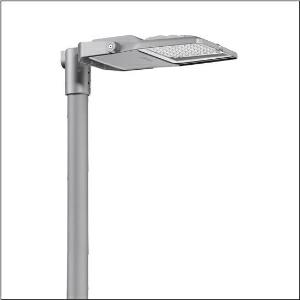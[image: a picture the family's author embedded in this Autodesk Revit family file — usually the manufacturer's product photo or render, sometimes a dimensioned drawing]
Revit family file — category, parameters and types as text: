
# Revit family: floodlight_fl_21_iq_mini___pl43_5xa7772b4a3a_1e53
name_source: partatom
category: Lighting Fixtures
units: mm (PartAtom-declared; Revit-internal decimal feet)

## family parameters
Cut with Voids When Loaded = No
Host = Face
Light Source = No
Part Type = Normal
Room Calculation Point = No
Round Connector Dimension = Use Diameter
Shared = No

## types (1)
- --- (1 x LED, 6660 lm, 45.5 W, 4000K)
    Apparent Load = 46 VA
    CIE Flux Codes = 27 78 99 100 100
    Color Rendering = 70
    Color Temperature = 4000K
    Default Elevation = 1800 mm
    Description = Floodlight FL 21 iQ mini, floodlight, primary light control with lens, of PMMA, primary optical cover: protective disc, of toughened safety glass, transparent, light distribution: PL43, light emission: direct distribution, installation type: surface-mounted, LED, High Power LED, rated luminous flux: 6.660lm, luminous efficacy: 146lm/W, light colour: 740, colour temperature: 4000K, control: Auto-Match, Temp-Guard, Night-Set, Smart-Wire, Desk-Remote (wireless, voltage-free reading and setting of iQ features in the workshop via application-optimized NFC function/RFID function), optimised constant luminous flux control (CLO 2.0), Light-Fading, Lumen-Switch, with terminal, 6-pole, mains connection: 220..240V, AC, 50/60Hz, start of lifetime: 46W, end of service life: 48W, reduction: 22W, luminaire housing, of diecast aluminium, powder-coated, Siteco® metallic grey (DB 702S), corrosivity category C5 mid according to DIN EN ISO 12944, sealing non-destructively replaceable, please order mast flange separately, mast bracket, of steel, galvanised, powder-coated, protection rating (complete): IP66, insulation class (complete): insulation class II (safety insulation), certification: CE, ENEC, VDE, protection symbol: D, impact resistance: IK08, permissible operating ambient temperature: -40..+40°C, permissible operating ambient temperature for outdoor applications: -40..+50°C, standard: DIN EN 12944, LABS conformity tested according to VDMA 24364:2018-05, packaging unit: 1 piece

Light Distribution: PL43
    Height = 70 mm
    Lamp = 1 x LED
    Lamp Light Flux = 6660 lm
    Lamp Power = 45.5 W
    Lamp count = 1
    Length = 485 mm
    Luminous efficacy = 146 lm/W
    Manufacturer = Siteco
    ModVariant = No
    Model = 5XA7772B4A3A
    Number of Poles = 1
    OnlyDefault = Yes
    Power Factor = 1
    Product Name = Floodlight FL 21 iQ mini | PL43
    Product group = floodlight | pylon annexe
    ProductGroupID = 6200
    Protection Class = Protection class II
    Protection Degree = IP 66
    RLX_Detail_Level = 1
    RLX_Emergency_Light_Flux = 0 lm
    RLX_Emergency_Type = 0
    RLX_Emergency_Type_DB = No
    RlxData = <blob elided: 101077 chars, md5=0e785a87>
    Socket = socket
    Standby Power = 0 W
    System Light Flux = 6660 lm
    System Power = 46 W
    Type Comments = factory setting: luminous flux: 100 % | dim-lin: 254 | 463 mA
    Type Image = l_1007125.jpg
    URL = http://relux.com
    VarID = @adj_112833
    Voltage = 0 V
    Weight = 0.00 kg
    Width = 337 mm

## geometry (parser evidence)
native form markers: Blend x4, Sweep x13
no freeform markers — native parametric forms only
